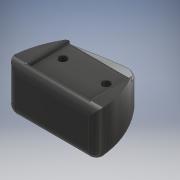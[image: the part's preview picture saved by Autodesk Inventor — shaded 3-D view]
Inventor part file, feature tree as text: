
AUTODESK INVENTOR PART (.ipt)
format: ipt  version: 2018 (Build 220112000, 112)  size: 223,744 bytes
history: native  units: mm
features: sketch x4, extrude x3, fillet x2, hole x1, mirror x1
ambient origin geometry x8: Origin, YZ Plane, XZ Plane, XY Plane, X Axis, Y Axis, Z Axis, Center Point
bodies: Solid1 (feature_tree)
feature tree (11):
  extrude  "Extrusion1"  Depth=22.5mm TaperAngle=0.0deg
  extrude  "Extrusion2"  Depth=50.0mm
  hole  "Hole1"  [1 undecoded]
  mirror  "Mirror1"
  extrude  "Extrusion3"  Depth=10.5mm
  fillet  "Fillet1"  Radius=10.0mm
  fillet  "Fillet2"  Radius=2.0mm
  sketch  "Sketch1"  dims[d0=44.0mm d1=22.5mm d2=0.0mm]
  sketch  "Sketch3"  dims[d3=30.0mm d4=50.0mm]
  sketch  "Sketch4"  dims[d5=4.0mm d6=2.0mm d7=0.0mm]
  sketch  "Sketch5"  dims[d9=12.0mm d10=10.5mm d11=4.0mm d12=6.0mm d13=4.0mm d14=2.0mm d15=90.0deg d16=10.0mm d17=20.594885mm d18=10.0mm d19=2.0mm d20=0.0mm d21=4.0mm d22=1.0mm]
note: 1 required parameter value undecoded (feature->parameter linkage not recoverable at this tier; creation-order binding heuristic only, values carry confidence <= 0.55)
